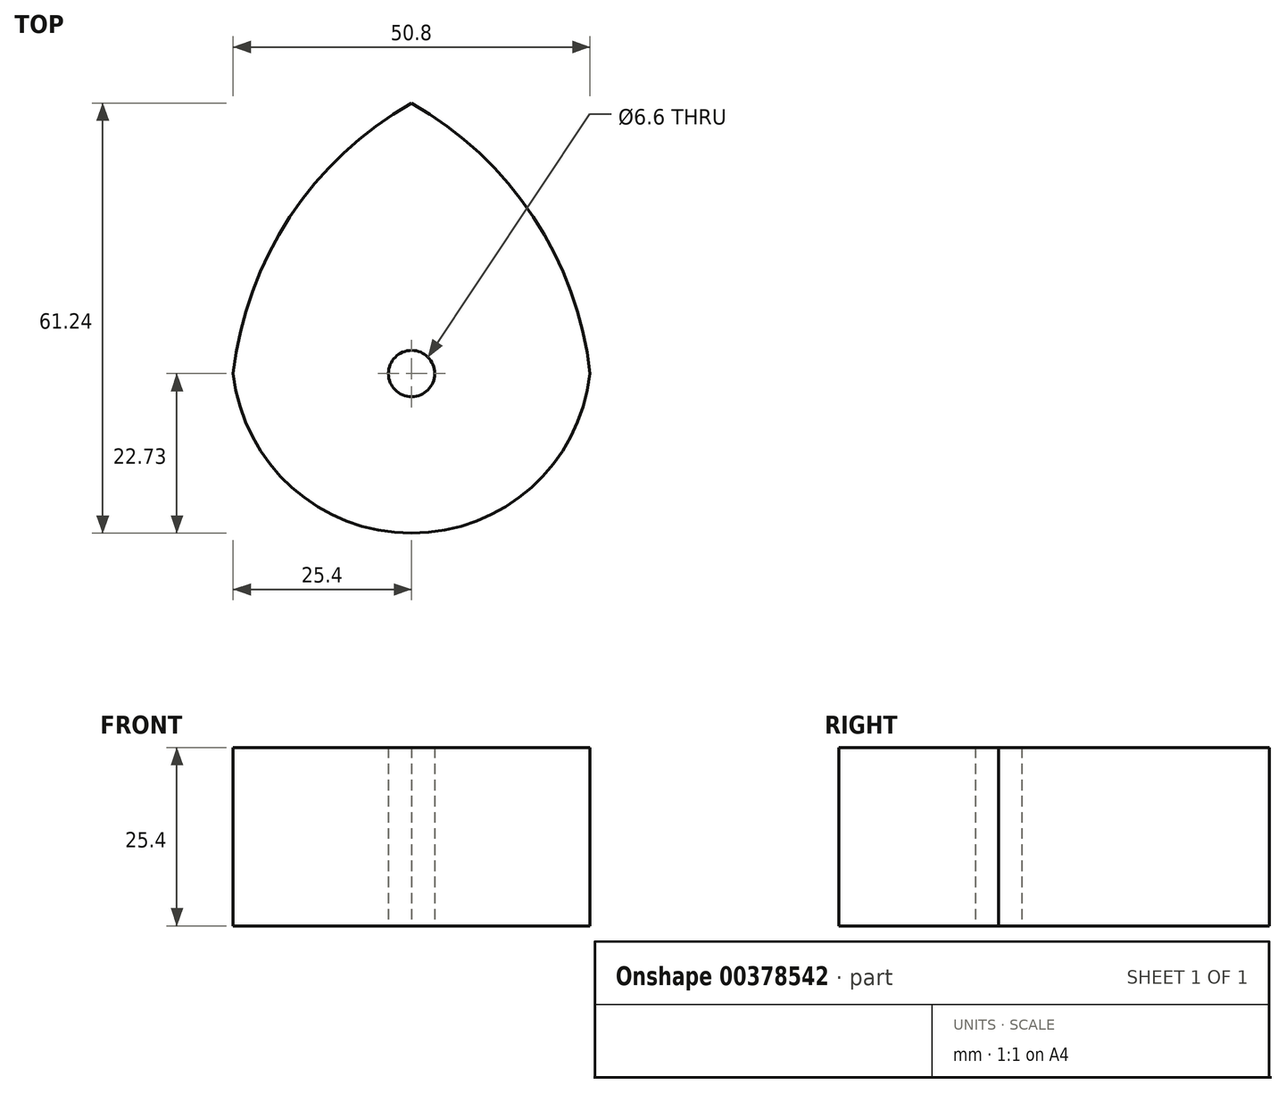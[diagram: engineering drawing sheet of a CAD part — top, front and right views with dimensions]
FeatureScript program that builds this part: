
annotation { "Feature Type Name" : "Feature", "Feature Type Description" : "" }
export const myFeature = defineFeature(function(context is Context, id is Id, definition is map)
    precondition{}
    {
        {
            var Q0;
            Q0=qCreatedBy(makeId("Top.planeOp"),FACE);
            var sketch = newSketch(context, id + "F0", { "sketchPlane" : qUnion([Q0])});
            skLineSegment(sketch, "E0", {"start": v(0, 0) * mm, "end": v(25.4, 0) * mm});
            skLineSegment(sketch, "E1", {"start": v(0, 0) * mm, "end": v(-25.4, 0) * mm});
            skArc(sketch, "E2", {"start": v(0, 38.51) * mm, "mid": v(-17.32, 22.3) * mm, "end": v(-25.4, 0) * mm});
            skArc(sketch, "E3", {"start": v(25.4, 0) * mm, "mid": v(17.32, 22.3) * mm, "end": v(0, 38.51) * mm});
            skArc(sketch, "E4", {"start": v(-25.4, 0) * mm, "mid": v(0, -22.73) * mm, "end": v(25.4, 0) * mm});
            skPoint(sketch, "E5.center.orphan", {"position": v(0, 7.3) * mm});
            skCircle(sketch, "E6", {"center": v(0, 0) * mm, "radius": 3.3 * mm});
            skSolve(sketch);
        }
        {
            var Q0;
            Q0 = qSketchRegion(id + "F0", true);
            extrude(context, id + "F1", {"entities" : qUnion([Q0]), "depth" : 25.4 * mm});
        }
    });
